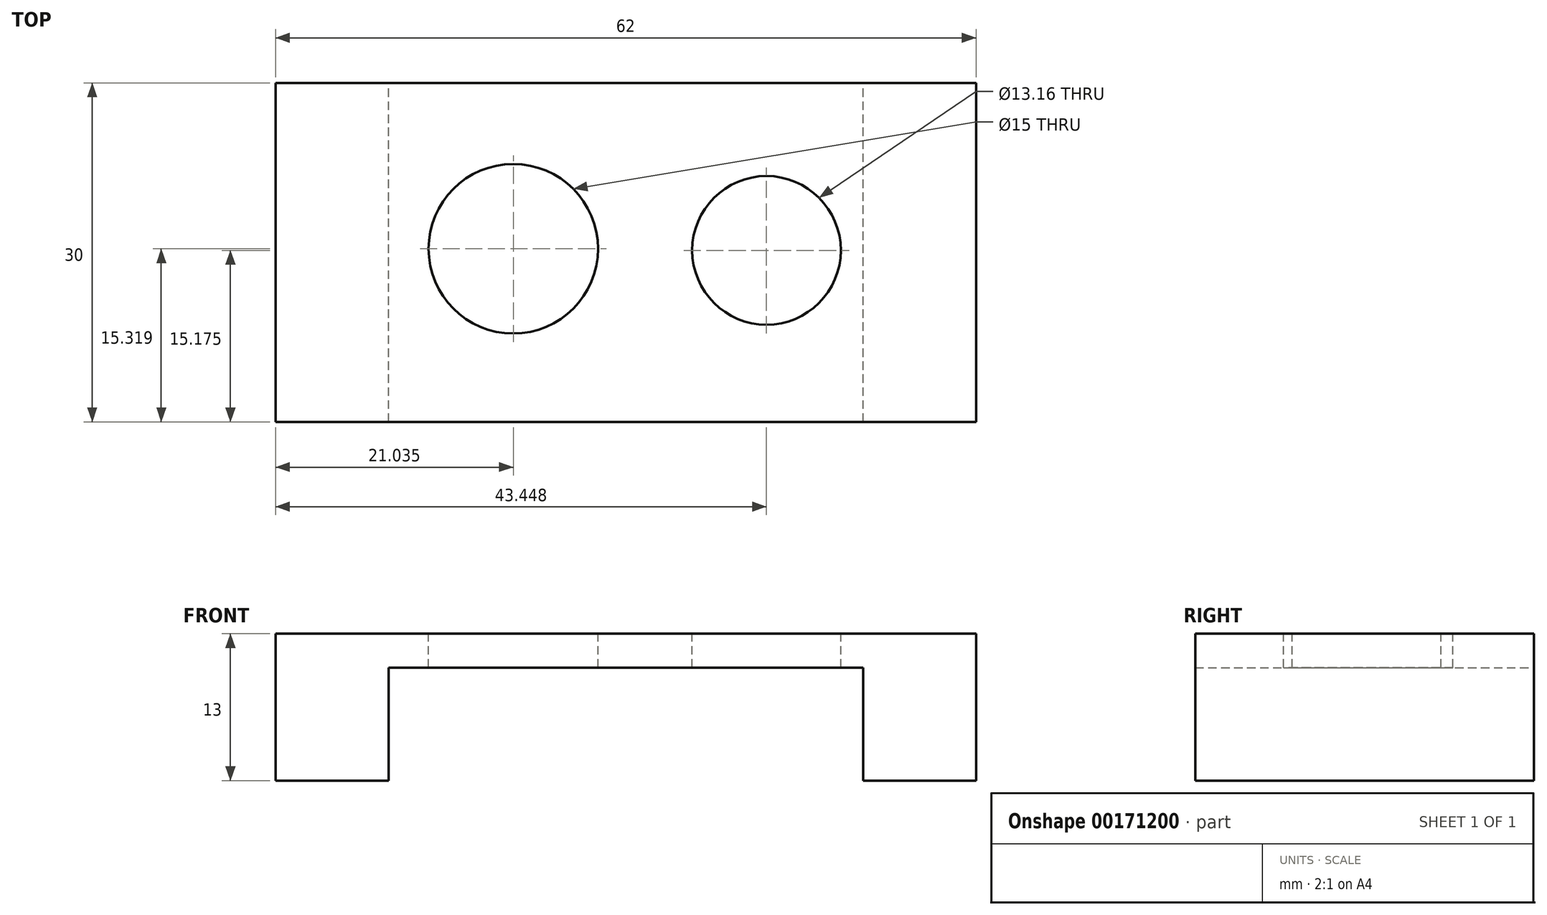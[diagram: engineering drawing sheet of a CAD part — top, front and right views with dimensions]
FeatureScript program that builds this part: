
annotation { "Feature Type Name" : "Feature", "Feature Type Description" : "" }
export const myFeature = defineFeature(function(context is Context, id is Id, definition is map)
    precondition{}
    {
        {
            var Q0;
            Q0=qCreatedBy(makeId("Front.planeOp"),FACE);
            var sketch = newSketch(context, id + "F0", { "sketchPlane" : qUnion([Q0])});
            skLineSegment(sketch, "E0", {"start": v(0, 0) * mm, "end": v(62, 0) * mm});
            skLineSegment(sketch, "E1", {"start": v(0, 0) * mm, "end": v(0, -13) * mm});
            skLineSegment(sketch, "E2", {"start": v(62, 0) * mm, "end": v(62, -13) * mm});
            skLineSegment(sketch, "E3", {"start": v(0, -13) * mm, "end": v(10, -13) * mm});
            skLineSegment(sketch, "E4", {"start": v(62, -13) * mm, "end": v(52, -13) * mm});
            skLineSegment(sketch, "E5", {"start": v(10, -13) * mm, "end": v(10, -3) * mm});
            skLineSegment(sketch, "E6", {"start": v(52, -13) * mm, "end": v(52, -3) * mm});
            skLineSegment(sketch, "E7", {"start": v(10, -3) * mm, "end": v(52, -3) * mm});
            skSolve(sketch);
        }
        {
            var Q0;
            Q0=qCreatedBy(makeId("Front.planeOp"),FACE);
            var sketch = newSketch(context, id + "F1", { "sketchPlane" : qUnion([Q0])});
            skSolve(sketch);
        }
        {
            var Q0;
            Q0 = qSketchRegion(id + "F1", true);
            var Q1;
            Q1=makeQuery(id+"F0.imprint","IMPRINT",FACE,{"disambiguationData":[TD([[makeQuery(id+"F0.imprint","IMPRINT",EDGE,{"derivedFrom":sQuery(id+"F0.wireOp",EDGE,"E0")}),-1.0]])]});
            extrude(context, id + "F2", {"entities" : qUnion([Q0, Q1]), "depth" : 30 * mm});
        }
        {
            var Q0;
            Q0=makeQuery(id+"F2.opExtrude","SWEPT_FACE",FACE,{"disambiguationData":[OSD([sQuery(id+"F0.wireOp",EDGE,"E0")])]});
            var sketch = newSketch(context, id + "F3", { "sketchPlane" : qUnion([Q0])});
            skCircle(sketch, "E8", {"center": v(21.03, -14.68) * mm, "radius": 7.5 * mm});
            skCircle(sketch, "E9", {"center": v(43.45, -14.83) * mm, "radius": 6.58 * mm});
            skSolve(sketch);
        }
        {
            var Q0;
            Q0=makeQuery(id+"F3.imprint","IMPRINT",FACE,{"disambiguationData":[TD([[makeQuery(id+"F3.imprint","IMPRINT",EDGE,{"derivedFrom":sQuery(id+"F3.wireOp",EDGE,"E8")}),1.0]])]});
            var Q1;
            Q1=makeQuery(id+"F3.imprint","IMPRINT",FACE,{"disambiguationData":[TD([[makeQuery(id+"F3.imprint","IMPRINT",EDGE,{"derivedFrom":sQuery(id+"F3.wireOp",EDGE,"E9")}),1.0]])]});
            extrude(context, id + "F4", {"entities" : qUnion([Q0, Q1]), "operationType" : NewBodyOperationType.REMOVE, "endBound" : BoundingType.THROUGH_ALL, "oppositeDirection" : true, "depth" : 25 * mm});
        }
    });
